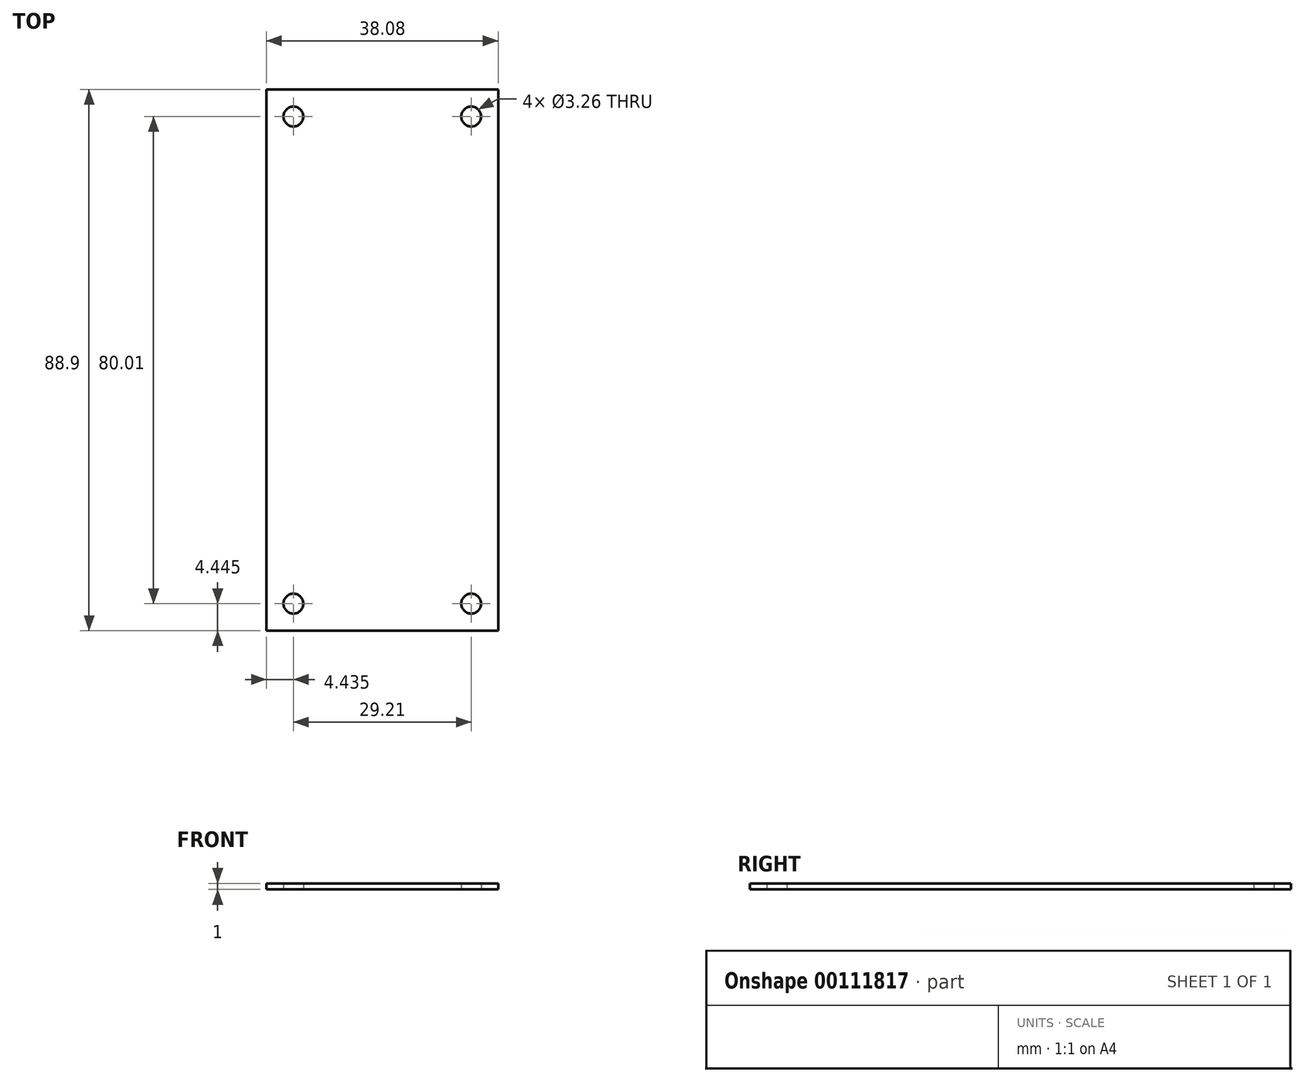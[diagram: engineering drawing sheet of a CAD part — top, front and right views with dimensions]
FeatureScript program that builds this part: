
annotation { "Feature Type Name" : "Feature", "Feature Type Description" : "" }
export const myFeature = defineFeature(function(context is Context, id is Id, definition is map)
    precondition{}
    {
        {
            var Q0;
            Q0=qCreatedBy(makeId("Top.planeOp"),FACE);
            var sketch = newSketch(context, id + "F0", { "sketchPlane" : qUnion([Q0])});
            skLineSegment(sketch, "E0.bottom", {"start": v(19.04, -44.45) * mm, "end": v(-19.04, -44.45) * mm});
            skLineSegment(sketch, "E0.top", {"start": v(19.04, 44.45) * mm, "end": v(-19.04, 44.45) * mm});
            skLineSegment(sketch, "E0.left", {"start": v(19.04, -44.45) * mm, "end": v(19.04, 44.45) * mm});
            skLineSegment(sketch, "E0.right", {"start": v(-19.04, -44.45) * mm, "end": v(-19.04, 44.45) * mm});
            skPoint(sketch, "E0.middle", {"position": v(0, 0) * mm});
            skLineSegment(sketch, "E1.bottom", {"start": v(14.6, -40) * mm, "end": v(-14.6, -40) * mm, "construction": true});
            skLineSegment(sketch, "E1.top", {"start": v(14.6, 40) * mm, "end": v(-14.6, 40) * mm, "construction": true});
            skLineSegment(sketch, "E1.left", {"start": v(14.6, -40) * mm, "end": v(14.6, 40) * mm, "construction": true});
            skLineSegment(sketch, "E1.right", {"start": v(-14.6, -40) * mm, "end": v(-14.6, 40) * mm, "construction": true});
            skCircle(sketch, "E2", {"center": v(-14.6, 40) * mm, "radius": 1.63 * mm});
            skCircle(sketch, "E3", {"center": v(14.6, 40) * mm, "radius": 1.63 * mm});
            skCircle(sketch, "E4", {"center": v(14.6, -40) * mm, "radius": 1.63 * mm});
            skCircle(sketch, "E5", {"center": v(-14.6, -40) * mm, "radius": 1.63 * mm});
            skSolve(sketch);
        }
        {
            var Q0;
            Q0 = qSketchRegion(id + "F0", true);
            extrude(context, id + "F1", {"entities" : qUnion([Q0]), "depth" : 1 * mm});
        }
    });
